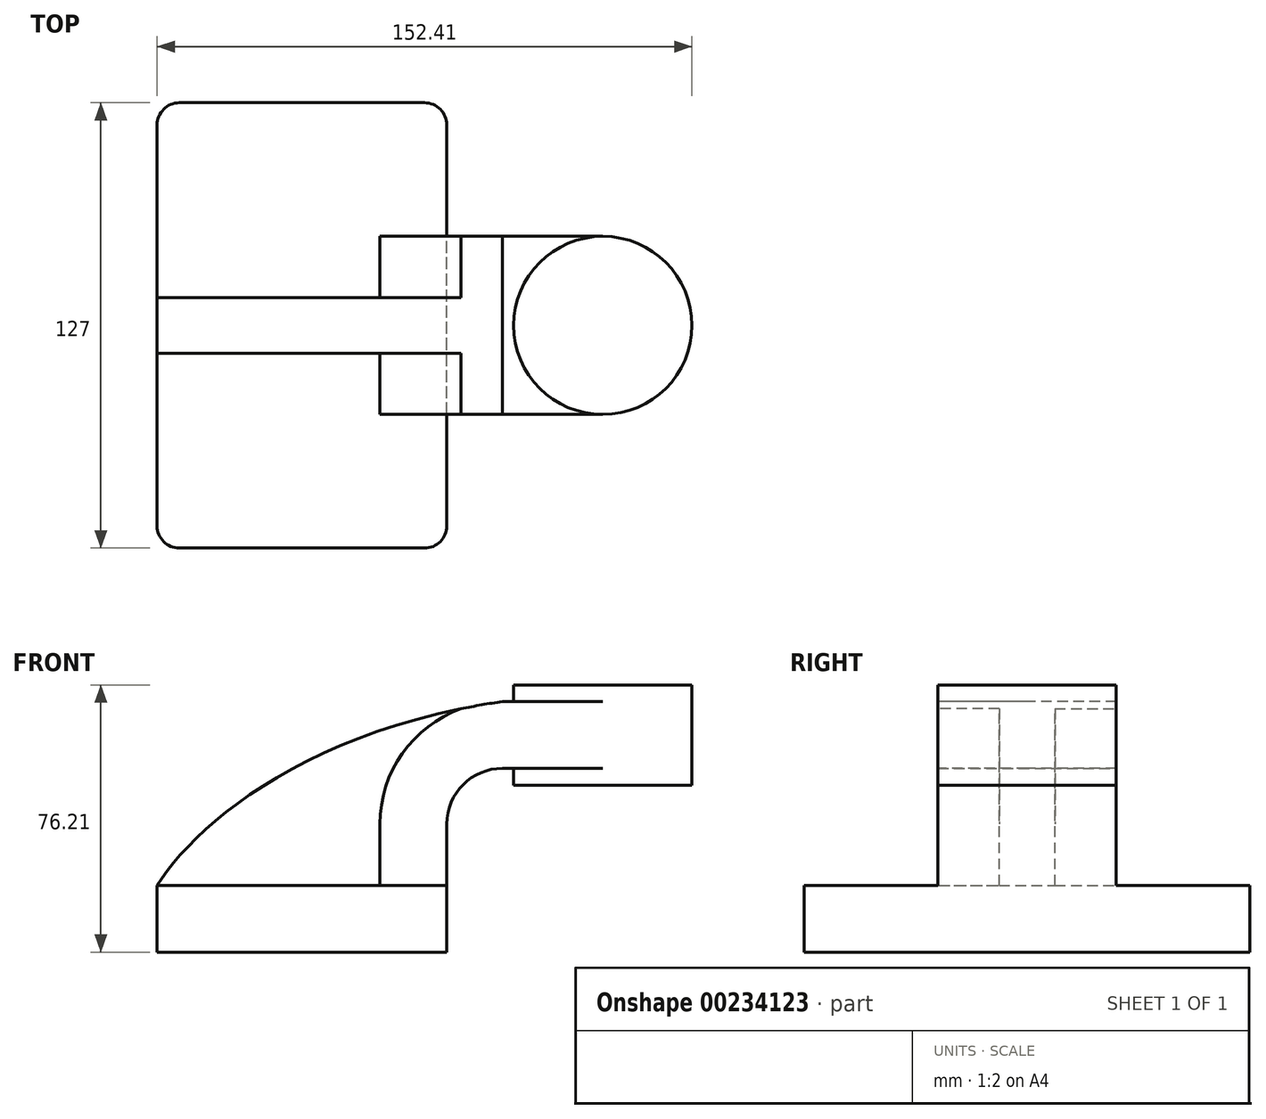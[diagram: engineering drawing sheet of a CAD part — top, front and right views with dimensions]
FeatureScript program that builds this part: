
annotation { "Feature Type Name" : "Feature", "Feature Type Description" : "" }
export const myFeature = defineFeature(function(context is Context, id is Id, definition is map)
    precondition{}
    {
        {
            var Q0;
            Q0=qCreatedBy(makeId("Front.planeOp"),FACE);
            var sketch = newSketch(context, id + "F0", { "sketchPlane" : qUnion([Q0])});
            skLineSegment(sketch, "E0.bottom", {"start": v(-41.28, -9.53) * mm, "end": v(41.28, -9.53) * mm});
            skLineSegment(sketch, "E0.top", {"start": v(-41.28, 9.53) * mm, "end": v(41.28, 9.53) * mm});
            skLineSegment(sketch, "E0.left", {"start": v(-41.28, -9.53) * mm, "end": v(-41.28, 9.53) * mm});
            skLineSegment(sketch, "E0.right", {"start": v(41.28, -9.53) * mm, "end": v(41.28, 9.53) * mm});
            skPoint(sketch, "E0.middle", {"position": v(0, 0) * mm});
            skLineSegment(sketch, "E1.bottom", {"start": v(111.12, 38.1) * mm, "end": v(60.32, 38.1) * mm});
            skLineSegment(sketch, "E1.top", {"start": v(111.12, 66.68) * mm, "end": v(60.33, 66.68) * mm});
            skLineSegment(sketch, "E1.left", {"start": v(111.12, 38.1) * mm, "end": v(111.12, 66.68) * mm});
            skLineSegment(sketch, "E1.right", {"start": v(60.32, 38.1) * mm, "end": v(60.32, 66.68) * mm});
            skPoint(sketch, "E1.middle", {"position": v(85.72, 52.39) * mm});
            skLineSegment(sketch, "E2", {"start": v(41.28, 9.53) * mm, "end": v(41.28, 27) * mm});
            skArc(sketch, "E3", {"start": v(41.27, 27) * mm, "mid": v(45.92, 38.23) * mm, "end": v(57.15, 42.88) * mm});
            skLineSegment(sketch, "E4", {"start": v(57.15, 42.88) * mm, "end": v(85.72, 42.88) * mm});
            skLineSegment(sketch, "E5.0", {"start": v(57.15, 61.93) * mm, "end": v(86.01, 61.93) * mm});
            skArc(sketch, "E5.1", {"start": v(22.22, 27) * mm, "mid": v(32.45, 51.7) * mm, "end": v(57.15, 61.93) * mm});
            skLineSegment(sketch, "E5.2", {"start": v(22.23, 9.53) * mm, "end": v(22.23, 27) * mm});
            skFitSpline(sketch, "E6", {"points": [v(-41.28, 9.53) * mm, v(57.15, 61.93) * mm], "startDerivative": vector(30.82, 49.18) * mm, "endDerivative": vector(171.45, 24.95) * mm});
            skPoint(sketch, "E7", {"position": v(85.72, 38.1) * mm});
            skLineSegment(sketch, "E8", {"start": v(85.72, 38.1) * mm, "end": v(85.72, 66.68) * mm});
            skSolve(sketch);
        }
        {
            var Q0;
            Q0=makeQuery(id+"F0.imprint","IMPRINT",FACE,{"disambiguationData":[TD([[makeQuery(id+"F0.imprint","IMPRINT",EDGE,{"derivedFrom":sQuery(id+"F0.wireOp",EDGE,"E0.bottom")}),1.0]])]});
            extrude(context, id + "F1", {"entities" : qUnion([Q0]), "endBound" : BoundingType.SYMMETRIC, "depth" : 127 * mm});
        }
        {
            var Q0;
            {var subQ6=sQuery(id+"F0.wireOp",EDGE,"E2");Q0=makeQuery(id+"F0.imprint","IMPRINT",FACE,{"disambiguationData":[TD([[makeQuery(id+"F0.imprint","IMPRINT",EDGE,{"derivedFrom":subQ6}),1.0]])]});}
            var Q1;
            {var subQ0=sQuery(id+"F0.wireOp",EDGE,"E4");var subQ1=sQuery(id+"F0.wireOp",EDGE,"E1.right");var subQ2=makeQuery(id+"F0.imprint","INTERSECT",VERTEX,{"derivedFrom":[subQ1,subQ0]});Q1=makeQuery(id+"F0.imprint","IMPRINT",FACE,{"disambiguationData":[TD([[makeQuery(id+"F0.imprint","IMPRINT",EDGE,{"disambiguationData":[TD([[subQ2,-1.0]])],"derivedFrom":subQ1}),-1.0]])]});}
            extrude(context, id + "F2", {"entities" : qUnion([Q0, Q1]), "operationType" : NewBodyOperationType.ADD, "endBound" : BoundingType.SYMMETRIC, "depth" : 50.8 * mm});
        }
        {
            var Q0;
            {var subQ3=sQuery(id+"F0.wireOp",EDGE,"E5.2");Q0=makeQuery(id+"F0.imprint","IMPRINT",FACE,{"disambiguationData":[TD([[makeQuery(id+"F0.imprint","IMPRINT",EDGE,{"derivedFrom":subQ3}),1.0]])]});}
            extrude(context, id + "F3", {"entities" : qUnion([Q0]), "operationType" : NewBodyOperationType.ADD, "endBound" : BoundingType.SYMMETRIC, "depth" : 15.88 * mm});
        }
        {
            var Q0;
            {var subQ4=sQuery(id+"F0.wireOp",EDGE,"E1.left");Q0=makeQuery(id+"F0.imprint","IMPRINT",FACE,{"disambiguationData":[TD([[makeQuery(id+"F0.imprint","IMPRINT",EDGE,{"derivedFrom":subQ4}),1.0]])]});}
            var Q1;
            Q1=sQuery(id+"F0.wireOp",EDGE,"E8");
            revolve(context, id + "F4", {"operationType" : NewBodyOperationType.ADD, "entities" : qUnion([Q0]), "axis" : qUnion([Q1]), "revolveType" : RevolveType.FULL});
        }
        {
            var Q0;
            Q0=makeQuery(id+"F1.opExtrude","CAP_EDGE",EDGE,{"disambiguationData":[OSD([sQuery(id+"F0.wireOp",EDGE,"E0.right")])],"isStart":false});
            var Q1;
            Q1=makeQuery(id+"F1.opExtrude","CAP_EDGE",EDGE,{"disambiguationData":[OSD([sQuery(id+"F0.wireOp",EDGE,"E0.left")])],"isStart":false});
            var Q2;
            Q2=makeQuery(id+"F1.opExtrude","CAP_EDGE",EDGE,{"disambiguationData":[OSD([sQuery(id+"F0.wireOp",EDGE,"E0.right")])],"isStart":true});
            var Q3;
            Q3=makeQuery(id+"F1.opExtrude","CAP_EDGE",EDGE,{"disambiguationData":[OSD([sQuery(id+"F0.wireOp",EDGE,"E0.left")])],"isStart":true});
            fillet(context, id + "F5", {"entities" : qUnion([Q0, Q1, Q2, Q3]), "radius" : 6.35 * mm, "tangentPropagation" : true, "allowEdgeOverflow" : false});
        }
    });
